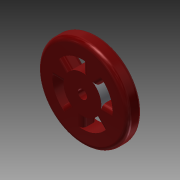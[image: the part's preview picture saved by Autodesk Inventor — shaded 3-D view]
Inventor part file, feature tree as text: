
AUTODESK INVENTOR PART (.ipt)
format: ipt  version: 2014 (Build 180170000, 170)  size: 219,136 bytes
history: native  units: mm
features: extrude x2, fillet x2, sketch x1
ambient origin geometry x8: Origin, YZ Plane, XZ Plane, XY Plane, X Axis, Y Axis, Z Axis, Center Point
bodies: Solid1 (feature_tree)
feature tree (5):
  sketch  "Sketch1"  dims[d0=6.0mm d1=60.0mm d2=10.0mm d3=0.0mm d4=25.0mm d5=40.0mm d7=45.0deg d8=10.0mm d9=0.0mm d10=3.0mm d11=3.0mm]
  extrude  "Extrusion1"  Depth=3.0mm
  extrude  "Extrusion2"  Depth=10.0mm TaperAngle=0.0deg
  fillet  "Fillet1"  Radius=25.0mm
  fillet  "Fillet2"  Radius=40.0mm
